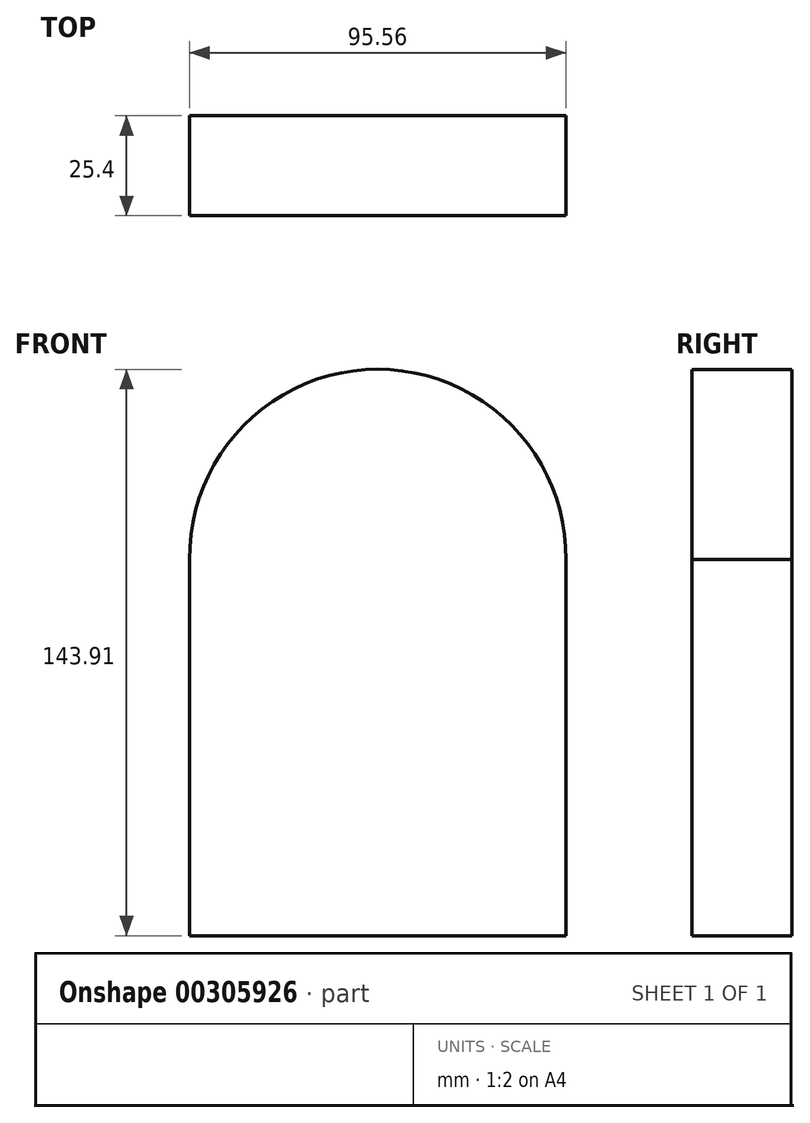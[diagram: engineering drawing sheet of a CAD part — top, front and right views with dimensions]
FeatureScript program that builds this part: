
annotation { "Feature Type Name" : "Feature", "Feature Type Description" : "" }
export const myFeature = defineFeature(function(context is Context, id is Id, definition is map)
    precondition{}
    {
        {
            var Q0;
            Q0=qCreatedBy(makeId("Front.planeOp"),FACE);
            var sketch = newSketch(context, id + "F0", { "sketchPlane" : qUnion([Q0])});
            skLineSegment(sketch, "E0.bottom", {"start": v(-47.78, 48.35) * mm, "end": v(47.78, 48.35) * mm});
            skLineSegment(sketch, "E0.top", {"start": v(-47.78, -48.35) * mm, "end": v(47.78, -48.35) * mm});
            skLineSegment(sketch, "E0.left", {"start": v(-47.78, 48.35) * mm, "end": v(-47.78, -48.35) * mm});
            skLineSegment(sketch, "E0.right", {"start": v(47.78, 48.35) * mm, "end": v(47.78, -48.35) * mm});
            skPoint(sketch, "E0.middle", {"position": v(0, 0) * mm});
            skCircle(sketch, "E1", {"center": v(0, 47.78) * mm, "radius": 47.78 * mm});
            skSolve(sketch);
        }
        {
            var Q0;
            {var subQ0=sQuery(id+"F0.wireOp",EDGE,"E0.bottom");Q0=makeQuery(id+"F0.imprint","IMPRINT",FACE,{"disambiguationData":[TD([[makeQuery(id+"F0.imprint","IMPRINT",EDGE,{"derivedFrom":subQ0}),1.0]])]});}
            var Q1;
            {var subQ0=sQuery(id+"F0.wireOp",EDGE,"E0.top");Q1=makeQuery(id+"F0.imprint","IMPRINT",FACE,{"disambiguationData":[TD([[makeQuery(id+"F0.imprint","IMPRINT",EDGE,{"derivedFrom":subQ0}),1.0]])]});}
            var Q2;
            {var subQ0=sQuery(id+"F0.wireOp",EDGE,"E1");var subQ1=sQuery(id+"F0.wireOp",EDGE,"E0.left");var subQ3=makeQuery(id+"F0.imprint","INTERSECT",VERTEX,{"derivedFrom":[subQ1,subQ0]});Q2=makeQuery(id+"F0.imprint","IMPRINT",FACE,{"disambiguationData":[TD([[makeQuery(id+"F0.imprint","IMPRINT",EDGE,{"disambiguationData":[TD([[subQ3,1.0]])],"derivedFrom":subQ1}),-1.0]])]});}
            var Q3;
            {var subQ0=sQuery(id+"F0.wireOp",EDGE,"E1");var subQ1=sQuery(id+"F0.wireOp",EDGE,"E0.right");var subQ3=makeQuery(id+"F0.imprint","INTERSECT",VERTEX,{"derivedFrom":[subQ1,subQ0]});Q3=makeQuery(id+"F0.imprint","IMPRINT",FACE,{"disambiguationData":[TD([[makeQuery(id+"F0.imprint","IMPRINT",EDGE,{"disambiguationData":[TD([[subQ3,1.0]])],"derivedFrom":subQ1}),1.0]])]});}
            var Q4;
            {var subQ0=sQuery(id+"F0.wireOp",EDGE,"E0.bottom");Q4=makeQuery(id+"F0.imprint","IMPRINT",FACE,{"disambiguationData":[TD([[makeQuery(id+"F0.imprint","IMPRINT",EDGE,{"derivedFrom":subQ0}),-1.0]])]});}
            extrude(context, id + "F1", {"entities" : qUnion([Q0, Q1, Q2, Q3, Q4]), "oppositeDirection" : true, "depth" : 25.4 * mm});
        }
    });
